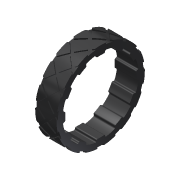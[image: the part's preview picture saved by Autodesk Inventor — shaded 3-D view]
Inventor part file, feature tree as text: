
AUTODESK INVENTOR PART (.ipt)
format: ipt  version: 2013 (Build 170138000, 138)  size: 927,232 bytes
history: native  units: in
note: dims shown in document units (in); Inventor stores cm internally (conversion verified against a paired STEP export)
features: extrude x1, mirror x1, imported_body x1, sketch x1
ambient origin geometry x8: Origin, YZ Plane, XZ Plane, XY Plane, X Axis, Y Axis, Z Axis, Center Point
bodies: Solid1 (feature_tree)
feature tree (4):
  extrude  "Extrusion1"  Depth=0.5in TaperAngle=0.0deg
  mirror  "Mirror1"
  imported_body  "Base1"
  sketch  "Sketch1"  dims[d0=4.5in d2=0.5in d3=0.0in]
